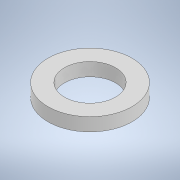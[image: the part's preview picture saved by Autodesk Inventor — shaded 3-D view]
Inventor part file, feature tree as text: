
AUTODESK INVENTOR PART (.ipt)
format: ipt  version: 2021 (Build 250183000, 183)  size: 97,792 bytes
history: native  units: mm
features: extrude x1, sketch x1
ambient origin geometry x8: Origin, YZ Plane, XZ Plane, XY Plane, X Axis, Y Axis, Z Axis, Center Point
bodies: Solid1 (feature_tree)
feature tree (2):
  extrude  "Extrusion1"  Depth=2.0mm
  sketch  "Sketch1"  dims[d0=7.75mm d1=2.5mm d2=2.0mm d3=0.0mm]
